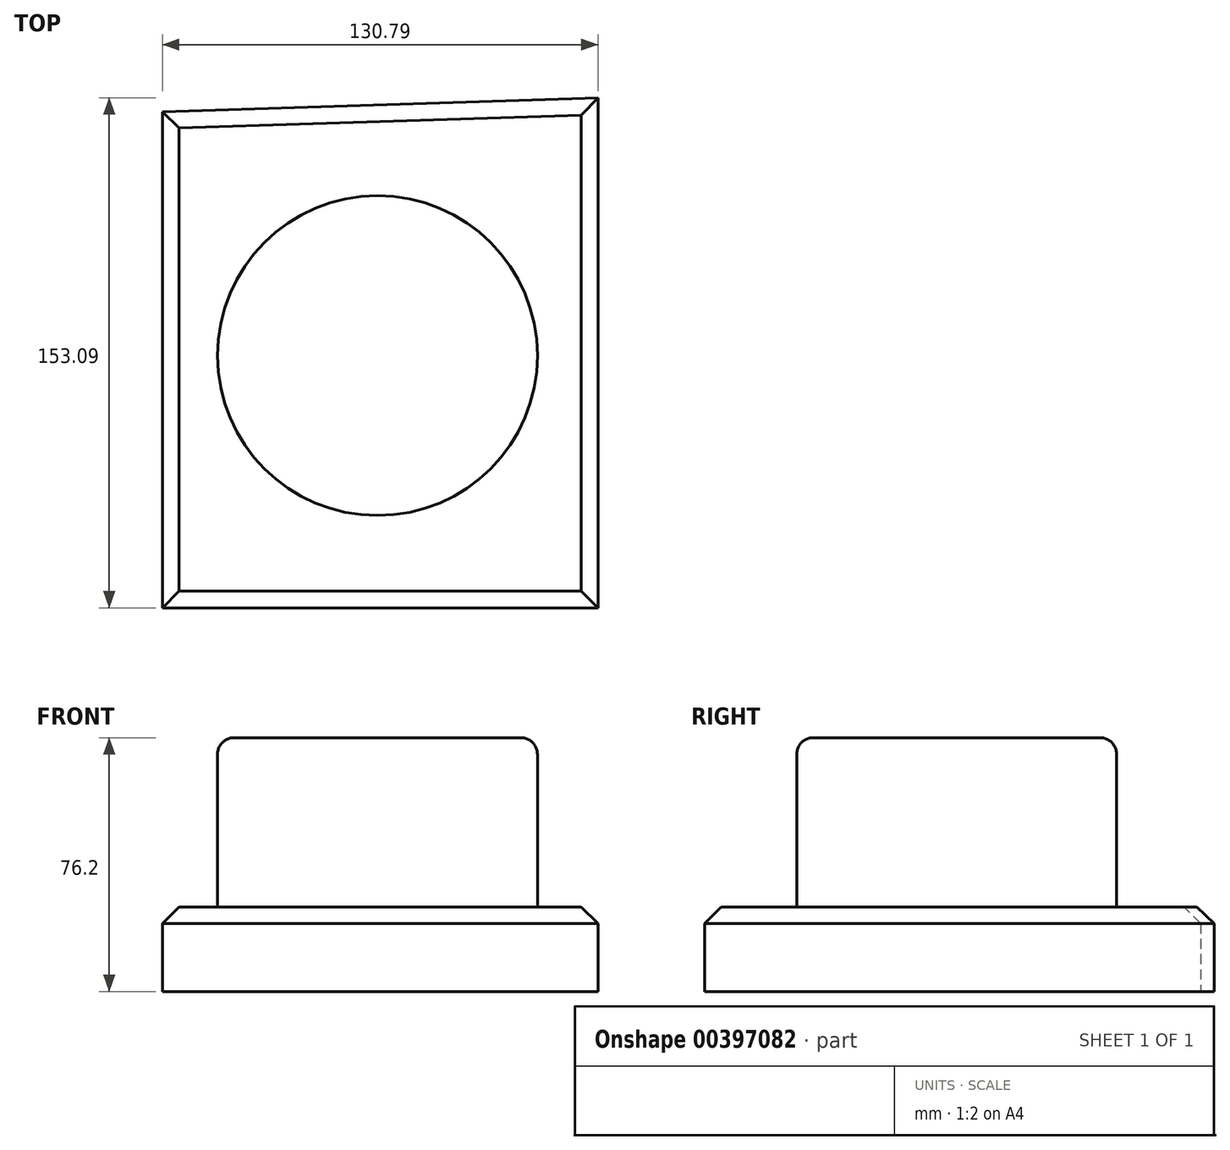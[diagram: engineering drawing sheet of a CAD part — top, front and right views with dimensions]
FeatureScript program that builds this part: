
annotation { "Feature Type Name" : "Feature", "Feature Type Description" : "" }
export const myFeature = defineFeature(function(context is Context, id is Id, definition is map)
    precondition{}
    {
        {
            var Q0;
            Q0=qCreatedBy(makeId("Top.planeOp"),FACE);
            var sketch = newSketch(context, id + "F0", { "sketchPlane" : qUnion([Q0])});
            skLineSegment(sketch, "E0", {"start": v(-12.62, -4.12) * mm, "end": v(-12.62, -153.1) * mm});
            skLineSegment(sketch, "E1", {"start": v(-12.62, -153.1) * mm, "end": v(118.17, -153.1) * mm});
            skLineSegment(sketch, "E2", {"start": v(118.17, -153.1) * mm, "end": v(118.17, 0) * mm});
            skLineSegment(sketch, "E3", {"start": v(118.17, 0) * mm, "end": v(-12.62, -4.12) * mm});
            skSolve(sketch);
        }
        {
            var Q0;
            Q0 = qSketchRegion(id + "F0", true);
            extrude(context, id + "F1", {"entities" : qUnion([Q0]), "depth" : 25.4 * mm});
        }
        {
            var Q0;
            Q0=makeQuery(id+"F1.opExtrude","CAP_FACE",FACE,{"disambiguationData":[OSD([sQuery(id+"F0.wireOp",EDGE,"E0"),sQuery(id+"F0.wireOp",EDGE,"E1"),sQuery(id+"F0.wireOp",EDGE,"E2"),sQuery(id+"F0.wireOp",EDGE,"E3")])],"isStart":false});
            var sketch = newSketch(context, id + "F2", { "sketchPlane" : qUnion([Q0])});
            skCircle(sketch, "E4", {"center": v(51.95, -77.36) * mm, "radius": 48.04 * mm});
            skSolve(sketch);
        }
        {
            var Q0;
            Q0 = qSketchRegion(id + "F2", true);
            extrude(context, id + "F3", {"entities" : qUnion([Q0]), "operationType" : NewBodyOperationType.ADD, "depth" : 50.8 * mm});
        }
        {
            var Q0;
            Q0=makeQuery(id+"F3.opExtrude","CAP_EDGE",EDGE,{"disambiguationData":[OSD([sQuery(id+"F2.wireOp",EDGE,"E4")])],"isStart":false});
            fillet(context, id + "F4", {"entities" : qUnion([Q0]), "radius" : 5 * mm, "tangentPropagation" : true, "allowEdgeOverflow" : false});
        }
        {
            var Q0;
            Q0=makeQuery(id+"F1.opExtrude","CAP_EDGE",EDGE,{"disambiguationData":[OSD([sQuery(id+"F0.wireOp",EDGE,"E2")])],"isStart":false});
            var Q1;
            Q1=makeQuery(id+"F1.opExtrude","CAP_EDGE",EDGE,{"disambiguationData":[OSD([sQuery(id+"F0.wireOp",EDGE,"E3")])],"isStart":false});
            var Q2;
            Q2=makeQuery(id+"F1.opExtrude","CAP_EDGE",EDGE,{"disambiguationData":[OSD([sQuery(id+"F0.wireOp",EDGE,"E0")])],"isStart":false});
            var Q3;
            Q3=makeQuery(id+"F1.opExtrude","CAP_EDGE",EDGE,{"disambiguationData":[OSD([sQuery(id+"F0.wireOp",EDGE,"E1")])],"isStart":false});
            chamfer(context, id + "F5", {"entities" : qUnion([Q0, Q1, Q2, Q3]), "width" : 5 * mm, "tangentPropagation" : true});
        }
        {
            var Q0;
            Q0=makeQuery(id+"F3.opExtrude","CAP_FACE",FACE,{"disambiguationData":[OSD([sQuery(id+"F2.wireOp",EDGE,"E4")])],"isStart":false});
            var sketch = newSketch(context, id + "F6", { "sketchPlane" : qUnion([Q0])});
            skCircle(sketch, "E5", {"center": v(51.95, -77.36) * mm, "radius": 9.45 * mm});
            skSolve(sketch);
        }
        {
            var Q0;
            Q0=sQuery(id+"F6.wireOp",EDGE,"E5");
            extrude(context, id + "F7", {"bodyType" : ToolBodyType.SURFACE, "surfaceEntities" : qUnion([Q0]), "depth" : 25 * mm});
        }
    });
